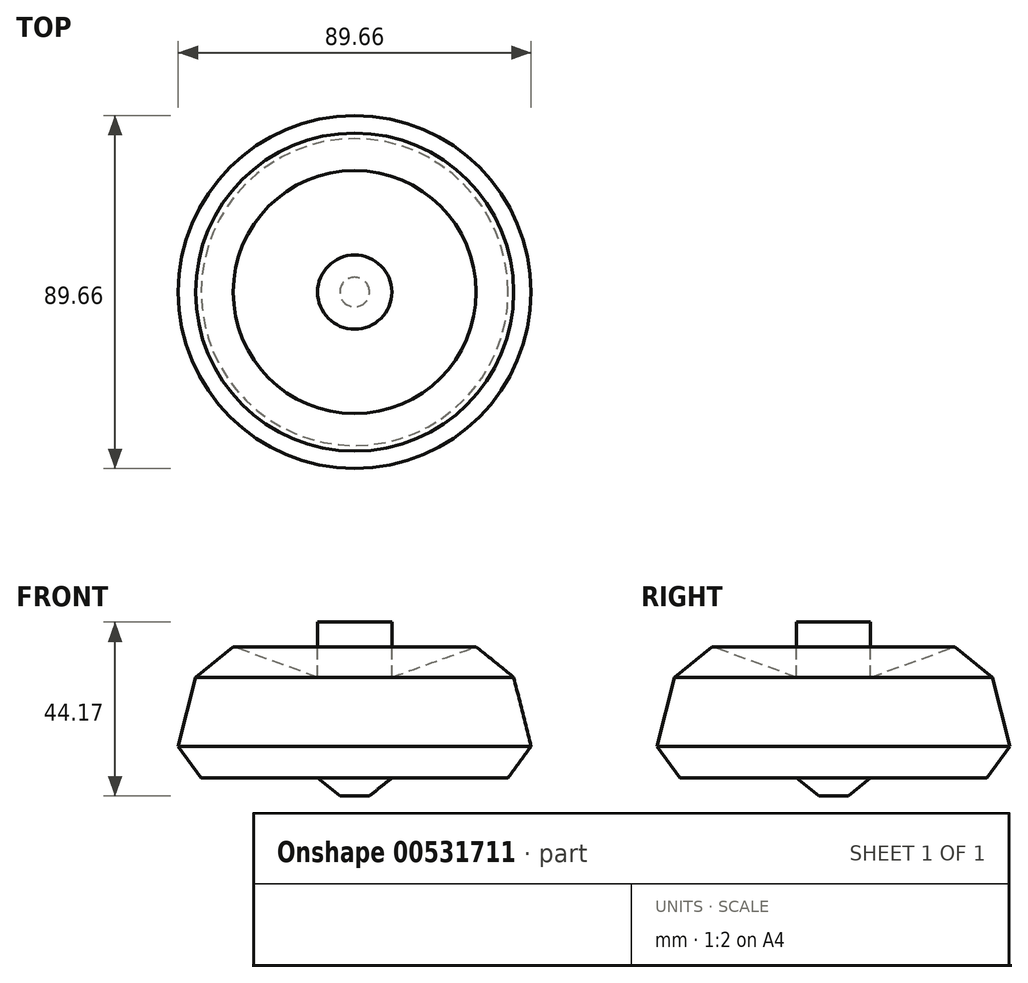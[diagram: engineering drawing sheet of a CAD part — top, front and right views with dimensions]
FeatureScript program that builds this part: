
annotation { "Feature Type Name" : "Feature", "Feature Type Description" : "" }
export const myFeature = defineFeature(function(context is Context, id is Id, definition is map)
    precondition{}
    {
        {
            var Q0;
            Q0=qCreatedBy(makeId("Front.planeOp"),FACE);
            var sketch = newSketch(context, id + "F0", { "sketchPlane" : qUnion([Q0])});
            skLineSegment(sketch, "E0", {"start": v(0, 0) * mm, "end": v(3.77, 0) * mm});
            skLineSegment(sketch, "E1", {"start": v(3.77, 0) * mm, "end": v(9.43, 4.56) * mm});
            skLineSegment(sketch, "E2", {"start": v(9.43, 4.56) * mm, "end": v(38.98, 4.56) * mm});
            skLineSegment(sketch, "E3", {"start": v(38.98, 4.56) * mm, "end": v(44.83, 12.6) * mm});
            skLineSegment(sketch, "E4", {"start": v(44.83, 12.6) * mm, "end": v(40.4, 30.13) * mm});
            skLineSegment(sketch, "E5", {"start": v(40.4, 30.13) * mm, "end": v(30.85, 37.9) * mm});
            skLineSegment(sketch, "E6", {"start": v(30.85, 37.9) * mm, "end": v(9.43, 30.13) * mm});
            skLineSegment(sketch, "E7", {"start": v(9.43, 30.13) * mm, "end": v(9.43, 44.17) * mm});
            skLineSegment(sketch, "E8", {"start": v(9.43, 44.17) * mm, "end": v(0, 44.17) * mm});
            skLineSegment(sketch, "E9", {"start": v(0, 44.17) * mm, "end": v(0, 0) * mm});
            skSolve(sketch);
        }
        {
            var Q0;
            Q0 = qSketchRegion(id + "F0", true);
            var Q1;
            Q1=sQuery(id+"F0.wireOp",EDGE,"E9");
            revolve(context, id + "F1", {"entities" : qUnion([Q0]), "axis" : qUnion([Q1]), "revolveType" : RevolveType.FULL});
        }
    });
